AUTODESK INVENTOR PART (.ipt)
format: ipt  version: 2016 (Build 200138000, 138)  size: 325,632 bytes
history: native  units: in
note: dims shown in document units (in); Inventor stores cm internally (conversion verified against a paired STEP export)
features: sketch x8, extrude x6, reference x5, chamfer x3, hole x2, other x1, pattern_circular x1, projected_geometry x1
ambient origin geometry x8: Origin, YZ Plane, XZ Plane, XY Plane, X Axis, Y Axis, Z Axis, Center Point
bodies: Solid1 (feature_tree)
feature tree (27):
  other  "Honlite Axes Adapter.ipt"
  extrude  "Extrusion1"  Depth=0.7988in TaperAngle=0.0deg
  hole  "Hole1"  [1 undecoded]
  hole  "Hole2"  [1 undecoded]
  extrude  "Extrusion3"  Depth=0.2362in
  extrude  "Extrusion4"  Depth=0.2362in
  extrude  "Extrusion5"  Depth=0.6181in TaperAngle=0.0deg
  chamfer  "Chamfer3"  Distance=0.2362in
  chamfer  "Chamfer1"  Distance=0.2362in
  extrude  "Extrusion6"  Depth=0.3937in
  pattern_circular  "Circular Pattern1"  [2 undecoded]
  extrude  "Extrusion7"  Depth=0.3937in TaperAngle=45.0deg
  chamfer  "Chamfer2"  Distance=0.3937in
  sketch  "Sketch1"  dims[d0=0.0236in d1=0.7988in d2=0.0in]
  reference  "Reference1"
  reference  "Reference2"
  reference  "Reference3"
  reference  "Reference4"
  reference  "Reference5"
  sketch  "Sketch2"  dims[d3=0.1339in d4=0.75in d5=0.375in d6=0.25in d7=0.5635in d8=1.0in d9=0.8108in d10=1.2205in]
  sketch  "Sketch3"  dims[d11=1.2205in]
  sketch  "Sketch5"  dims[d12=0.1339in d13=0.75in d14=0.375in d15=0.25in d16=0.5635in d17=1.0in d18=0.8108in d22=0.9055in]
  sketch  "Sketch6"  dims[d23=0.2756in d24=0.0in d25=0.2362in]
  sketch  "Sketch7"  dims[d26=0.2362in d28=0.2362in]
  sketch  "Sketch8"  dims[d29=0.2362in d30=0.6181in d31=0.0in]
  projected_geometry  "Projected Loop1"
  sketch  "Sketch9"  dims[d32=0.2362in d33=0.2362in d34=0.2362in d35=0.2362in d36=0.6181in d37=0.0in d38=0.0472in d39=0.0787in d40=45.0deg d41=0.3937in d66=0.4567in d42=0.5906in d43=0.3937in d44=0.0in d45=1.5748in d46=360.0deg d49=0.0787in d50=0.6732in d51=0.0in d52=0.0787in d53=0.0787in d54=45.0deg d55=0.0787in d56=0.0787in d57=45.0deg d58=0.3937in]
note: 4 required parameter values undecoded (feature->parameter linkage not recoverable at this tier; creation-order binding heuristic only, values carry confidence <= 0.55)
